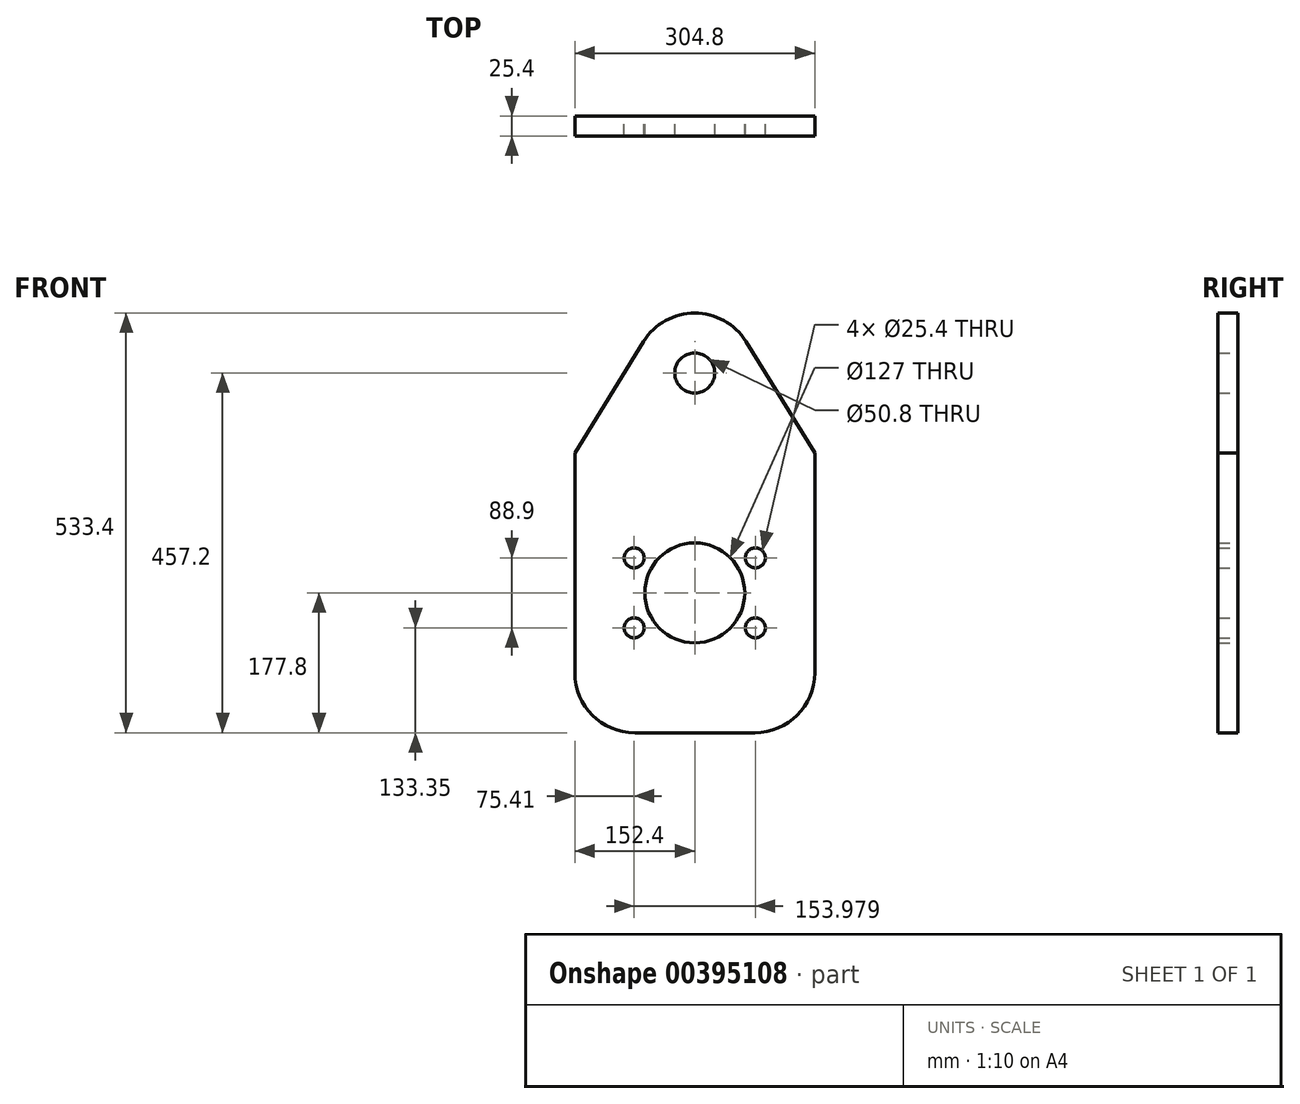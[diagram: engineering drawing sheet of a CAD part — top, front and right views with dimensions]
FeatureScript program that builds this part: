
annotation { "Feature Type Name" : "Feature", "Feature Type Description" : "" }
export const myFeature = defineFeature(function(context is Context, id is Id, definition is map)
    precondition{}
    {
        {
            var Q0;
            Q0=qCreatedBy(makeId("Front.planeOp"),FACE);
            var sketch = newSketch(context, id + "F0", { "sketchPlane" : qUnion([Q0])});
            skLineSegment(sketch, "E0.left", {"start": v(-152.4, 177.8) * mm, "end": v(-152.4, -101.6) * mm});
            skLineSegment(sketch, "E0.right", {"start": v(152.4, 177.8) * mm, "end": v(152.4, -101.6) * mm});
            skPoint(sketch, "E0.middle", {"position": v(0, 0) * mm});
            skArc(sketch, "E1", {"start": v(64.81, 319.47) * mm, "mid": v(0, 355.6) * mm, "end": v(-64.81, 319.47) * mm});
            skLineSegment(sketch, "E2", {"start": v(-64.81, 319.47) * mm, "end": v(-152.4, 177.8) * mm});
            skLineSegment(sketch, "E3", {"start": v(64.81, 319.47) * mm, "end": v(152.4, 177.8) * mm});
            skCircle(sketch, "E4", {"center": v(0, 0) * mm, "radius": 63.5 * mm});
            skCircle(sketch, "E5.1.0", {"center": v(-76.99, 44.45) * mm, "radius": 12.7 * mm});
            skCircle(sketch, "E5.2.0", {"center": v(-76.99, -44.45) * mm, "radius": 12.7 * mm});
            skCircle(sketch, "E5.4.0", {"center": v(76.99, -44.45) * mm, "radius": 12.7 * mm});
            skCircle(sketch, "E5.5.0", {"center": v(76.99, 44.45) * mm, "radius": 12.7 * mm});
            skCircle(sketch, "E6", {"center": v(0, 279.4) * mm, "radius": 25.4 * mm});
            skPoint(sketch, "E7.center.orphan", {"position": v(0, -177.8) * mm});
            skLineSegment(sketch, "E8", {"start": v(-76.2, -177.8) * mm, "end": v(76.2, -177.8) * mm});
            skPoint(sketch, "E9.orphan", {"position": v(-152.4, -177.8) * mm});
            skPoint(sketch, "E10.orphan", {"position": v(152.4, -177.8) * mm});
            skArc(sketch, "E11.filletArc", {"start": v(-152.4, -101.6) * mm, "mid": v(-130.08, -155.48) * mm, "end": v(-76.2, -177.8) * mm});
            skArc(sketch, "E12.filletArc", {"start": v(76.2, -177.8) * mm, "mid": v(130.08, -155.48) * mm, "end": v(152.4, -101.6) * mm});
            skLineSegment(sketch, "E13", {"start": v(0, -177.8) * mm, "end": v(0, 403.9) * mm, "construction": true});
            skPoint(sketch, "E14.center.orphan", {"position": v(0, 88.9) * mm});
            skSolve(sketch);
        }
        {
            var Q0;
            Q0 = qSketchRegion(id + "F0", true);
            extrude(context, id + "F1", {"entities" : qUnion([Q0]), "depth" : 25.4 * mm});
        }
    });
